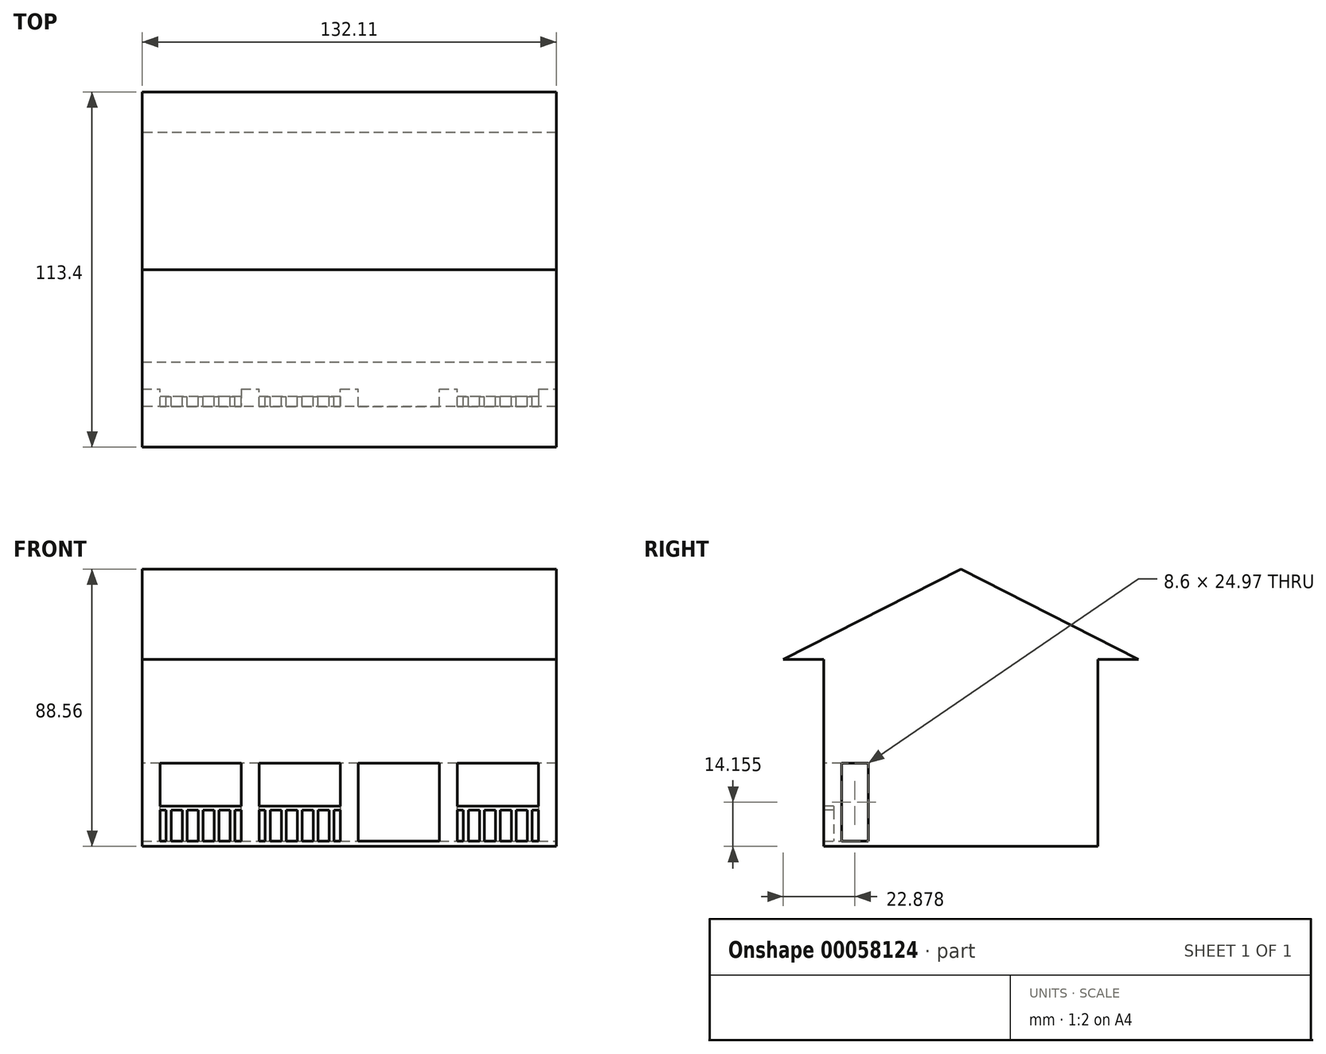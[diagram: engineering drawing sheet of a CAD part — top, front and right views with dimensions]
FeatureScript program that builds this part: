
annotation { "Feature Type Name" : "Feature", "Feature Type Description" : "" }
export const myFeature = defineFeature(function(context is Context, id is Id, definition is map)
    precondition{}
    {
        {
            var Q0;
            Q0=qCreatedBy(makeId("Right.planeOp"),FACE);
            var sketch = newSketch(context, id + "F0", { "sketchPlane" : qUnion([Q0])});
            skLineSegment(sketch, "E0.bottom", {"start": v(-28.53, -15.4) * mm, "end": v(58.95, -15.4) * mm});
            skLineSegment(sketch, "E0.top", {"start": v(-28.53, 44.37) * mm, "end": v(58.95, 44.37) * mm});
            skLineSegment(sketch, "E0.left", {"start": v(-28.53, -15.4) * mm, "end": v(-28.53, 44.37) * mm});
            skLineSegment(sketch, "E0.right", {"start": v(58.95, -15.4) * mm, "end": v(58.95, 44.37) * mm});
            skLineSegment(sketch, "E1", {"start": v(-28.53, 44.37) * mm, "end": v(-41.49, 44.37) * mm});
            skLineSegment(sketch, "E2", {"start": v(-41.49, 44.37) * mm, "end": v(15.2, 73.17) * mm});
            skLineSegment(sketch, "E3", {"start": v(15.2, 73.17) * mm, "end": v(71.9, 44.37) * mm});
            skLineSegment(sketch, "E4", {"start": v(71.9, 44.37) * mm, "end": v(58.95, 44.37) * mm});
            skLineSegment(sketch, "E5", {"start": v(-14.3, -15.4) * mm, "end": v(-14.3, 11.25) * mm});
            skLineSegment(sketch, "E6", {"start": v(-14.3, 11.25) * mm, "end": v(-28.53, 11.25) * mm});
            skSolve(sketch);
        }
        {
            var Q0;
            Q0=makeQuery(id+"F0.imprint","IMPRINT",FACE,{"disambiguationData":[TD([[makeQuery(id+"F0.imprint","IMPRINT",EDGE,{"derivedFrom":sQuery(id+"F0.wireOp",EDGE,"E0.top")}),1.0]])]});
            var Q1;
            {var subQ2=sQuery(id+"F0.wireOp",EDGE,"E0.top");Q1=makeQuery(id+"F0.imprint","IMPRINT",FACE,{"disambiguationData":[TD([[makeQuery(id+"F0.imprint","IMPRINT",EDGE,{"derivedFrom":subQ2}),-1.0]])]});}
            extrude(context, id + "F1", {"entities" : qUnion([Q0, Q1]), "depth" : 132.11 * mm});
        }
        {
            var Q0;
            Q0=makeQuery(id+"F1.opExtrude","SWEPT_FACE",FACE,{"disambiguationData":[OSD([sQuery(id+"F0.wireOp",EDGE,"E5")])]});
            var sketch = newSketch(context, id + "F2", { "sketchPlane" : qUnion([Q0])});
            skLineSegment(sketch, "E7.bottom", {"start": v(0, -15.4) * mm, "end": v(132.11, -15.4) * mm});
            skLineSegment(sketch, "E7.top", {"start": v(0, -13.72) * mm, "end": v(132.11, -13.72) * mm});
            skLineSegment(sketch, "E7.left", {"start": v(0, -15.4) * mm, "end": v(0, -13.72) * mm});
            skLineSegment(sketch, "E7.right", {"start": v(132.11, -15.4) * mm, "end": v(132.11, -13.72) * mm});
            skSolve(sketch);
        }
        {
            var Q0;
            Q0=makeQuery(id+"F2.imprint","IMPRINT",FACE,{"disambiguationData":[TD([[makeQuery(id+"F2.imprint","IMPRINT",EDGE,{"derivedFrom":sQuery(id+"F2.wireOp",EDGE,"E7.bottom")}),-1.0]])]});
            var Q1;
            Q1=makeQuery(id+"F1.opExtrude","SWEPT_FACE",FACE,{"disambiguationData":[OSD([sQuery(id+"F0.wireOp",EDGE,"E0.left")])]});
            extrude(context, id + "F3", {"entities" : qUnion([Q0]), "operationType" : NewBodyOperationType.ADD, "endBound" : BoundingType.UP_TO_SURFACE, "endBoundEntityFace" : qUnion([Q1]), "depth" : 25.4 * mm});
        }
        {
            var Q0;
            Q0=makeQuery(id+"F3.opExtrude","SWEPT_FACE",FACE,{"disambiguationData":[OSD([sQuery(id+"F2.wireOp",EDGE,"E7.top")])]});
            var sketch = newSketch(context, id + "F4", { "sketchPlane" : qUnion([Q0])});
            skLineSegment(sketch, "E8.bottom", {"start": v(0, -28.53) * mm, "end": v(5.62, -28.53) * mm});
            skLineSegment(sketch, "E8.top", {"start": v(0, -22.91) * mm, "end": v(5.62, -22.91) * mm});
            skLineSegment(sketch, "E8.left", {"start": v(0, -28.53) * mm, "end": v(0, -22.91) * mm});
            skLineSegment(sketch, "E8.right", {"start": v(5.62, -28.53) * mm, "end": v(5.62, -22.91) * mm});
            skLineSegment(sketch, "E9.1.0.0", {"start": v(31.62, -28.53) * mm, "end": v(37.24, -28.53) * mm});
            skLineSegment(sketch, "E9.1.0.1", {"start": v(31.62, -22.91) * mm, "end": v(37.24, -22.91) * mm});
            skLineSegment(sketch, "E9.1.0.2", {"start": v(31.62, -28.53) * mm, "end": v(31.62, -22.91) * mm});
            skLineSegment(sketch, "E9.1.0.3", {"start": v(37.24, -28.53) * mm, "end": v(37.24, -22.91) * mm});
            skLineSegment(sketch, "E9.2.0.0", {"start": v(63.25, -28.53) * mm, "end": v(68.86, -28.53) * mm});
            skLineSegment(sketch, "E9.2.0.1", {"start": v(63.25, -22.91) * mm, "end": v(68.86, -22.91) * mm});
            skLineSegment(sketch, "E9.2.0.2", {"start": v(63.25, -28.53) * mm, "end": v(63.25, -22.91) * mm});
            skLineSegment(sketch, "E9.2.0.3", {"start": v(68.86, -28.53) * mm, "end": v(68.86, -22.91) * mm});
            skLineSegment(sketch, "E9.3.0.0", {"start": v(94.87, -28.53) * mm, "end": v(100.49, -28.53) * mm});
            skLineSegment(sketch, "E9.3.0.1", {"start": v(94.87, -22.91) * mm, "end": v(100.49, -22.91) * mm});
            skLineSegment(sketch, "E9.3.0.2", {"start": v(94.87, -28.53) * mm, "end": v(94.87, -22.91) * mm});
            skLineSegment(sketch, "E9.3.0.3", {"start": v(100.49, -28.53) * mm, "end": v(100.49, -22.91) * mm});
            skLineSegment(sketch, "E9.4.0.0", {"start": v(126.5, -28.53) * mm, "end": v(132.11, -28.53) * mm});
            skLineSegment(sketch, "E9.4.0.1", {"start": v(126.5, -22.91) * mm, "end": v(132.11, -22.91) * mm});
            skLineSegment(sketch, "E9.4.0.2", {"start": v(126.5, -28.53) * mm, "end": v(126.5, -22.91) * mm});
            skLineSegment(sketch, "E9.4.0.3", {"start": v(132.11, -28.53) * mm, "end": v(132.11, -22.91) * mm});
            skLineSegment(sketch, "E9.direction1", {"start": v(0, -28.53) * mm, "end": v(31.62, -28.53) * mm, "construction": true});
            skLineSegment(sketch, "E10.bottom", {"start": v(7.63, -28.53) * mm, "end": v(9.26, -28.53) * mm});
            skLineSegment(sketch, "E10.top", {"start": v(7.63, -25.42) * mm, "end": v(9.26, -25.42) * mm});
            skLineSegment(sketch, "E10.left", {"start": v(7.63, -28.53) * mm, "end": v(7.63, -25.42) * mm});
            skLineSegment(sketch, "E10.right", {"start": v(9.26, -28.53) * mm, "end": v(9.26, -25.42) * mm});
            skLineSegment(sketch, "E11.1.0.0", {"start": v(12.72, -25.42) * mm, "end": v(14.35, -25.42) * mm});
            skLineSegment(sketch, "E11.1.0.1", {"start": v(12.72, -28.53) * mm, "end": v(14.35, -28.53) * mm});
            skLineSegment(sketch, "E11.1.0.2", {"start": v(14.35, -28.53) * mm, "end": v(14.35, -25.42) * mm});
            skLineSegment(sketch, "E11.1.0.3", {"start": v(12.72, -28.53) * mm, "end": v(12.72, -25.42) * mm});
            skLineSegment(sketch, "E11.2.0.0", {"start": v(17.8, -25.42) * mm, "end": v(19.43, -25.42) * mm});
            skLineSegment(sketch, "E11.2.0.1", {"start": v(17.8, -28.53) * mm, "end": v(19.43, -28.53) * mm});
            skLineSegment(sketch, "E11.2.0.2", {"start": v(19.43, -28.53) * mm, "end": v(19.43, -25.42) * mm});
            skLineSegment(sketch, "E11.2.0.3", {"start": v(17.8, -28.53) * mm, "end": v(17.8, -25.42) * mm});
            skLineSegment(sketch, "E11.3.0.0", {"start": v(22.9, -25.42) * mm, "end": v(24.52, -25.42) * mm});
            skLineSegment(sketch, "E11.3.0.1", {"start": v(22.9, -28.53) * mm, "end": v(24.52, -28.53) * mm});
            skLineSegment(sketch, "E11.3.0.2", {"start": v(24.52, -28.53) * mm, "end": v(24.52, -25.42) * mm});
            skLineSegment(sketch, "E11.3.0.3", {"start": v(22.9, -28.53) * mm, "end": v(22.9, -25.42) * mm});
            skLineSegment(sketch, "E11.4.0.0", {"start": v(27.98, -25.42) * mm, "end": v(29.6, -25.42) * mm});
            skLineSegment(sketch, "E11.4.0.1", {"start": v(27.98, -28.53) * mm, "end": v(29.6, -28.53) * mm});
            skLineSegment(sketch, "E11.4.0.2", {"start": v(29.6, -28.53) * mm, "end": v(29.6, -25.42) * mm});
            skLineSegment(sketch, "E11.4.0.3", {"start": v(27.98, -28.53) * mm, "end": v(27.98, -25.42) * mm});
            skLineSegment(sketch, "E11.direction1", {"start": v(7.63, -25.42) * mm, "end": v(12.72, -25.42) * mm, "construction": true});
            skLineSegment(sketch, "E12", {"start": v(7.63, -25.42) * mm, "end": v(5.62, -25.42) * mm, "construction": true});
            skLineSegment(sketch, "E13", {"start": v(29.6, -25.42) * mm, "end": v(31.62, -25.42) * mm, "construction": true});
            skLineSegment(sketch, "E14.1.0.0", {"start": v(44.34, -28.53) * mm, "end": v(45.97, -28.53) * mm});
            skLineSegment(sketch, "E14.1.0.1", {"start": v(49.43, -25.42) * mm, "end": v(51.06, -25.42) * mm});
            skLineSegment(sketch, "E14.1.0.2", {"start": v(39.26, -25.42) * mm, "end": v(44.34, -25.42) * mm, "construction": true});
            skLineSegment(sketch, "E14.1.0.3", {"start": v(44.34, -25.42) * mm, "end": v(45.97, -25.42) * mm});
            skLineSegment(sketch, "E14.1.0.4", {"start": v(54.51, -28.53) * mm, "end": v(56.14, -28.53) * mm});
            skLineSegment(sketch, "E14.1.0.5", {"start": v(54.51, -25.42) * mm, "end": v(56.14, -25.42) * mm});
            skLineSegment(sketch, "E14.1.0.6", {"start": v(59.6, -28.53) * mm, "end": v(59.6, -25.42) * mm});
            skLineSegment(sketch, "E14.1.0.7", {"start": v(39.26, -28.53) * mm, "end": v(40.89, -28.53) * mm});
            skLineSegment(sketch, "E14.1.0.8", {"start": v(39.26, -28.53) * mm, "end": v(39.26, -25.42) * mm});
            skLineSegment(sketch, "E14.1.0.9", {"start": v(59.6, -25.42) * mm, "end": v(61.23, -25.42) * mm});
            skLineSegment(sketch, "E14.1.0.10", {"start": v(49.43, -28.53) * mm, "end": v(51.06, -28.53) * mm});
            skLineSegment(sketch, "E14.1.0.11", {"start": v(59.6, -28.53) * mm, "end": v(61.23, -28.53) * mm});
            skLineSegment(sketch, "E14.1.0.12", {"start": v(39.26, -25.42) * mm, "end": v(40.89, -25.42) * mm});
            skLineSegment(sketch, "E14.1.0.13", {"start": v(49.43, -28.53) * mm, "end": v(49.43, -25.42) * mm});
            skLineSegment(sketch, "E14.1.0.14", {"start": v(45.97, -28.53) * mm, "end": v(45.97, -25.42) * mm});
            skLineSegment(sketch, "E14.1.0.15", {"start": v(54.51, -28.53) * mm, "end": v(54.51, -25.42) * mm});
            skLineSegment(sketch, "E14.1.0.16", {"start": v(56.14, -28.53) * mm, "end": v(56.14, -25.42) * mm});
            skLineSegment(sketch, "E14.1.0.17", {"start": v(40.89, -28.53) * mm, "end": v(40.89, -25.42) * mm});
            skLineSegment(sketch, "E14.1.0.18", {"start": v(61.23, -28.53) * mm, "end": v(61.23, -25.42) * mm});
            skLineSegment(sketch, "E14.1.0.19", {"start": v(44.34, -28.53) * mm, "end": v(44.34, -25.42) * mm});
            skLineSegment(sketch, "E14.1.0.20", {"start": v(51.06, -28.53) * mm, "end": v(51.06, -25.42) * mm});
            skLineSegment(sketch, "E14.2.0.0", {"start": v(75.97, -28.53) * mm, "end": v(77.6, -28.53) * mm});
            skLineSegment(sketch, "E14.2.0.1", {"start": v(81.05, -25.42) * mm, "end": v(82.68, -25.42) * mm});
            skLineSegment(sketch, "E14.2.0.2", {"start": v(70.88, -25.42) * mm, "end": v(75.97, -25.42) * mm, "construction": true});
            skLineSegment(sketch, "E14.2.0.3", {"start": v(75.97, -25.42) * mm, "end": v(77.6, -25.42) * mm});
            skLineSegment(sketch, "E14.2.0.4", {"start": v(86.14, -28.53) * mm, "end": v(87.77, -28.53) * mm});
            skLineSegment(sketch, "E14.2.0.5", {"start": v(86.14, -25.42) * mm, "end": v(87.77, -25.42) * mm});
            skLineSegment(sketch, "E14.2.0.6", {"start": v(91.22, -28.53) * mm, "end": v(91.22, -25.42) * mm});
            skLineSegment(sketch, "E14.2.0.7", {"start": v(70.88, -28.53) * mm, "end": v(72.5, -28.53) * mm});
            skLineSegment(sketch, "E14.2.0.8", {"start": v(70.88, -28.53) * mm, "end": v(70.88, -25.42) * mm});
            skLineSegment(sketch, "E14.2.0.9", {"start": v(91.22, -25.42) * mm, "end": v(92.85, -25.42) * mm});
            skLineSegment(sketch, "E14.2.0.10", {"start": v(81.05, -28.53) * mm, "end": v(82.68, -28.53) * mm});
            skLineSegment(sketch, "E14.2.0.11", {"start": v(91.22, -28.53) * mm, "end": v(92.85, -28.53) * mm});
            skLineSegment(sketch, "E14.2.0.12", {"start": v(70.88, -25.42) * mm, "end": v(72.5, -25.42) * mm});
            skLineSegment(sketch, "E14.2.0.13", {"start": v(81.05, -28.53) * mm, "end": v(81.05, -25.42) * mm});
            skLineSegment(sketch, "E14.2.0.14", {"start": v(77.6, -28.53) * mm, "end": v(77.6, -25.42) * mm});
            skLineSegment(sketch, "E14.2.0.15", {"start": v(86.14, -28.53) * mm, "end": v(86.14, -25.42) * mm});
            skLineSegment(sketch, "E14.2.0.16", {"start": v(87.77, -28.53) * mm, "end": v(87.77, -25.42) * mm});
            skLineSegment(sketch, "E14.2.0.17", {"start": v(72.5, -28.53) * mm, "end": v(72.5, -25.42) * mm});
            skLineSegment(sketch, "E14.2.0.18", {"start": v(92.85, -28.53) * mm, "end": v(92.85, -25.42) * mm});
            skLineSegment(sketch, "E14.2.0.19", {"start": v(75.97, -28.53) * mm, "end": v(75.97, -25.42) * mm});
            skLineSegment(sketch, "E14.2.0.20", {"start": v(82.68, -28.53) * mm, "end": v(82.68, -25.42) * mm});
            skLineSegment(sketch, "E14.3.0.0", {"start": v(107.59, -28.53) * mm, "end": v(109.22, -28.53) * mm});
            skLineSegment(sketch, "E14.3.0.1", {"start": v(112.68, -25.42) * mm, "end": v(114.3, -25.42) * mm});
            skLineSegment(sketch, "E14.3.0.2", {"start": v(102.5, -25.42) * mm, "end": v(107.59, -25.42) * mm, "construction": true});
            skLineSegment(sketch, "E14.3.0.3", {"start": v(107.59, -25.42) * mm, "end": v(109.22, -25.42) * mm});
            skLineSegment(sketch, "E14.3.0.4", {"start": v(117.76, -28.53) * mm, "end": v(119.4, -28.53) * mm});
            skLineSegment(sketch, "E14.3.0.5", {"start": v(117.76, -25.42) * mm, "end": v(119.4, -25.42) * mm});
            skLineSegment(sketch, "E14.3.0.6", {"start": v(122.85, -28.53) * mm, "end": v(122.85, -25.42) * mm});
            skLineSegment(sketch, "E14.3.0.7", {"start": v(102.5, -28.53) * mm, "end": v(104.13, -28.53) * mm});
            skLineSegment(sketch, "E14.3.0.8", {"start": v(102.5, -28.53) * mm, "end": v(102.5, -25.42) * mm});
            skLineSegment(sketch, "E14.3.0.9", {"start": v(122.85, -25.42) * mm, "end": v(124.48, -25.42) * mm});
            skLineSegment(sketch, "E14.3.0.10", {"start": v(112.68, -28.53) * mm, "end": v(114.3, -28.53) * mm});
            skLineSegment(sketch, "E14.3.0.11", {"start": v(122.85, -28.53) * mm, "end": v(124.48, -28.53) * mm});
            skLineSegment(sketch, "E14.3.0.12", {"start": v(102.5, -25.42) * mm, "end": v(104.13, -25.42) * mm});
            skLineSegment(sketch, "E14.3.0.13", {"start": v(112.68, -28.53) * mm, "end": v(112.68, -25.42) * mm});
            skLineSegment(sketch, "E14.3.0.14", {"start": v(109.22, -28.53) * mm, "end": v(109.22, -25.42) * mm});
            skLineSegment(sketch, "E14.3.0.15", {"start": v(117.76, -28.53) * mm, "end": v(117.76, -25.42) * mm});
            skLineSegment(sketch, "E14.3.0.16", {"start": v(119.4, -28.53) * mm, "end": v(119.4, -25.42) * mm});
            skLineSegment(sketch, "E14.3.0.17", {"start": v(104.13, -28.53) * mm, "end": v(104.13, -25.42) * mm});
            skLineSegment(sketch, "E14.3.0.18", {"start": v(124.48, -28.53) * mm, "end": v(124.48, -25.42) * mm});
            skLineSegment(sketch, "E14.3.0.19", {"start": v(107.59, -28.53) * mm, "end": v(107.59, -25.42) * mm});
            skLineSegment(sketch, "E14.3.0.20", {"start": v(114.3, -28.53) * mm, "end": v(114.3, -25.42) * mm});
            skLineSegment(sketch, "E14.direction1", {"start": v(12.72, -28.53) * mm, "end": v(44.34, -28.53) * mm, "construction": true});
            skLineSegment(sketch, "E15", {"start": v(39.26, -25.42) * mm, "end": v(37.24, -25.42) * mm, "construction": true});
            skSolve(sketch);
        }
        {
            var Q0;
            Q0=makeQuery(id+"F4.imprint","IMPRINT",FACE,{"disambiguationData":[TD([[makeQuery(id+"F4.imprint","IMPRINT",EDGE,{"derivedFrom":sQuery(id+"F4.wireOp",EDGE,"E8.bottom")}),1.0]])]});
            var Q1;
            Q1=makeQuery(id+"F4.imprint","IMPRINT",FACE,{"disambiguationData":[TD([[makeQuery(id+"F4.imprint","IMPRINT",EDGE,{"derivedFrom":sQuery(id+"F4.wireOp",EDGE,"E9.1.0.0")}),1.0]])]});
            var Q2;
            Q2=makeQuery(id+"F4.imprint","IMPRINT",FACE,{"disambiguationData":[TD([[makeQuery(id+"F4.imprint","IMPRINT",EDGE,{"derivedFrom":sQuery(id+"F4.wireOp",EDGE,"E9.2.0.0")}),1.0]])]});
            var Q3;
            Q3=makeQuery(id+"F4.imprint","IMPRINT",FACE,{"disambiguationData":[TD([[makeQuery(id+"F4.imprint","IMPRINT",EDGE,{"derivedFrom":sQuery(id+"F4.wireOp",EDGE,"E9.3.0.0")}),1.0]])]});
            var Q4;
            Q4=makeQuery(id+"F4.imprint","IMPRINT",FACE,{"disambiguationData":[TD([[makeQuery(id+"F4.imprint","IMPRINT",EDGE,{"derivedFrom":sQuery(id+"F4.wireOp",EDGE,"E9.4.0.0")}),1.0]])]});
            extrude(context, id + "F5", {"entities" : qUnion([Q0, Q1, Q2, Q3, Q4]), "operationType" : NewBodyOperationType.ADD, "endBound" : BoundingType.UP_TO_NEXT, "depth" : 25.4 * mm});
        }
        {
            var Q0;
            Q0=makeQuery(id+"F4.imprint","IMPRINT",FACE,{"disambiguationData":[TD([[makeQuery(id+"F4.imprint","IMPRINT",EDGE,{"derivedFrom":sQuery(id+"F4.wireOp",EDGE,"E8.bottom")}),1.0]])]});
            var Q1;
            Q1=makeQuery(id+"F4.imprint","IMPRINT",FACE,{"disambiguationData":[TD([[makeQuery(id+"F4.imprint","IMPRINT",EDGE,{"derivedFrom":sQuery(id+"F4.wireOp",EDGE,"E9.1.0.0")}),1.0]])]});
            var Q2;
            Q2=makeQuery(id+"F4.imprint","IMPRINT",FACE,{"disambiguationData":[TD([[makeQuery(id+"F4.imprint","IMPRINT",EDGE,{"derivedFrom":sQuery(id+"F4.wireOp",EDGE,"E9.2.0.0")}),1.0]])]});
            var Q3;
            Q3=makeQuery(id+"F4.imprint","IMPRINT",FACE,{"disambiguationData":[TD([[makeQuery(id+"F4.imprint","IMPRINT",EDGE,{"derivedFrom":sQuery(id+"F4.wireOp",EDGE,"E9.3.0.0")}),1.0]])]});
            var Q4;
            Q4=makeQuery(id+"F4.imprint","IMPRINT",FACE,{"disambiguationData":[TD([[makeQuery(id+"F4.imprint","IMPRINT",EDGE,{"derivedFrom":sQuery(id+"F4.wireOp",EDGE,"E9.4.0.0")}),1.0]])]});
            var Q5;
            Q5=makeQuery(id+"F4.imprint","IMPRINT",FACE,{"disambiguationData":[TD([[makeQuery(id+"F4.imprint","IMPRINT",EDGE,{"derivedFrom":sQuery(id+"F4.wireOp",EDGE,"E10.bottom")}),1.0]])]});
            var Q6;
            Q6=makeQuery(id+"F4.imprint","IMPRINT",FACE,{"disambiguationData":[TD([[makeQuery(id+"F4.imprint","IMPRINT",EDGE,{"derivedFrom":sQuery(id+"F4.wireOp",EDGE,"E11.1.0.0")}),-1.0]])]});
            var Q7;
            Q7=makeQuery(id+"F4.imprint","IMPRINT",FACE,{"disambiguationData":[TD([[makeQuery(id+"F4.imprint","IMPRINT",EDGE,{"derivedFrom":sQuery(id+"F4.wireOp",EDGE,"E11.2.0.0")}),-1.0]])]});
            var Q8;
            Q8=makeQuery(id+"F4.imprint","IMPRINT",FACE,{"disambiguationData":[TD([[makeQuery(id+"F4.imprint","IMPRINT",EDGE,{"derivedFrom":sQuery(id+"F4.wireOp",EDGE,"E11.3.0.0")}),-1.0]])]});
            var Q9;
            Q9=makeQuery(id+"F4.imprint","IMPRINT",FACE,{"disambiguationData":[TD([[makeQuery(id+"F4.imprint","IMPRINT",EDGE,{"derivedFrom":sQuery(id+"F4.wireOp",EDGE,"E11.4.0.0")}),-1.0]])]});
            var Q10;
            Q10=makeQuery(id+"F4.imprint","IMPRINT",FACE,{"disambiguationData":[TD([[makeQuery(id+"F4.imprint","IMPRINT",EDGE,{"derivedFrom":sQuery(id+"F4.wireOp",EDGE,"E14.1.0.0")}),1.0]])]});
            var Q11;
            Q11=makeQuery(id+"F4.imprint","IMPRINT",FACE,{"disambiguationData":[TD([[makeQuery(id+"F4.imprint","IMPRINT",EDGE,{"derivedFrom":sQuery(id+"F4.wireOp",EDGE,"E14.1.0.1")}),-1.0]])]});
            var Q12;
            Q12=makeQuery(id+"F4.imprint","IMPRINT",FACE,{"disambiguationData":[TD([[makeQuery(id+"F4.imprint","IMPRINT",EDGE,{"derivedFrom":sQuery(id+"F4.wireOp",EDGE,"E14.1.0.4")}),1.0]])]});
            var Q13;
            Q13=makeQuery(id+"F4.imprint","IMPRINT",FACE,{"disambiguationData":[TD([[makeQuery(id+"F4.imprint","IMPRINT",EDGE,{"derivedFrom":sQuery(id+"F4.wireOp",EDGE,"E14.1.0.6")}),-1.0]])]});
            var Q14;
            Q14=makeQuery(id+"F4.imprint","IMPRINT",FACE,{"disambiguationData":[TD([[makeQuery(id+"F4.imprint","IMPRINT",EDGE,{"derivedFrom":sQuery(id+"F4.wireOp",EDGE,"E14.1.0.7")}),1.0]])]});
            var Q15;
            Q15=makeQuery(id+"F4.imprint","IMPRINT",FACE,{"disambiguationData":[TD([[makeQuery(id+"F4.imprint","IMPRINT",EDGE,{"derivedFrom":sQuery(id+"F4.wireOp",EDGE,"E14.3.0.0")}),1.0]])]});
            var Q16;
            Q16=makeQuery(id+"F4.imprint","IMPRINT",FACE,{"disambiguationData":[TD([[makeQuery(id+"F4.imprint","IMPRINT",EDGE,{"derivedFrom":sQuery(id+"F4.wireOp",EDGE,"E14.3.0.1")}),-1.0]])]});
            var Q17;
            Q17=makeQuery(id+"F4.imprint","IMPRINT",FACE,{"disambiguationData":[TD([[makeQuery(id+"F4.imprint","IMPRINT",EDGE,{"derivedFrom":sQuery(id+"F4.wireOp",EDGE,"E14.3.0.4")}),1.0]])]});
            var Q18;
            Q18=makeQuery(id+"F4.imprint","IMPRINT",FACE,{"disambiguationData":[TD([[makeQuery(id+"F4.imprint","IMPRINT",EDGE,{"derivedFrom":sQuery(id+"F4.wireOp",EDGE,"E14.3.0.6")}),-1.0]])]});
            var Q19;
            Q19=makeQuery(id+"F4.imprint","IMPRINT",FACE,{"disambiguationData":[TD([[makeQuery(id+"F4.imprint","IMPRINT",EDGE,{"derivedFrom":sQuery(id+"F4.wireOp",EDGE,"E14.3.0.7")}),1.0]])]});
            extrude(context, id + "F6", {"entities" : qUnion([Q0, Q1, Q2, Q3, Q4, Q5, Q6, Q7, Q8, Q9, Q10, Q11, Q12, Q13, Q14, Q15, Q16, Q17, Q18, Q19]), "operationType" : NewBodyOperationType.ADD, "depth" : 10 * mm});
        }
        {
            var Q0;
            Q0=makeQuery(id+"F5.opExtrude","SWEPT_FACE",FACE,{"disambiguationData":[OSD([sQuery(id+"F4.wireOp",EDGE,"E8.right")])]});
            var sketch = newSketch(context, id + "F7", { "sketchPlane" : qUnion([Q0])});
            skLineSegment(sketch, "E16.bottom", {"start": v(-28.53, -3.72) * mm, "end": v(-25.42, -3.72) * mm});
            skLineSegment(sketch, "E16.top", {"start": v(-28.53, -2.48) * mm, "end": v(-25.42, -2.48) * mm});
            skLineSegment(sketch, "E16.left", {"start": v(-28.53, -3.72) * mm, "end": v(-28.53, -2.48) * mm});
            skLineSegment(sketch, "E16.right", {"start": v(-25.42, -3.72) * mm, "end": v(-25.42, -2.48) * mm});
            skSolve(sketch);
        }
        {
            var Q0;
            Q0=makeQuery(id+"F7.imprint","IMPRINT",FACE,{"disambiguationData":[TD([[makeQuery(id+"F7.imprint","IMPRINT",EDGE,{"derivedFrom":sQuery(id+"F7.wireOp",EDGE,"E16.bottom")}),1.0]])]});
            var Q1;
            Q1=makeQuery(id+"F5.opExtrude","SWEPT_FACE",FACE,{"disambiguationData":[OSD([sQuery(id+"F4.wireOp",EDGE,"E9.2.0.2")])]});
            extrude(context, id + "F8", {"entities" : qUnion([Q0]), "operationType" : NewBodyOperationType.ADD, "endBound" : BoundingType.UP_TO_SURFACE, "endBoundEntityFace" : qUnion([Q1]), "depth" : 25.4 * mm});
        }
        {
            var Q0;
            Q0=makeQuery(id+"F5.opExtrude","SWEPT_FACE",FACE,{"disambiguationData":[OSD([sQuery(id+"F4.wireOp",EDGE,"E9.3.0.3")])]});
            var sketch = newSketch(context, id + "F9", { "sketchPlane" : qUnion([Q0])});
            skLineSegment(sketch, "E17.0", {"start": v(-28.53, -2.48) * mm, "end": v(-25.42, -2.48) * mm});
            skLineSegment(sketch, "E17.1", {"start": v(-28.53, -3.72) * mm, "end": v(-28.53, -2.48) * mm});
            skLineSegment(sketch, "E17.2", {"start": v(-28.53, -3.72) * mm, "end": v(-25.42, -3.72) * mm});
            skLineSegment(sketch, "E17.3", {"start": v(-25.42, -3.72) * mm, "end": v(-25.42, -2.48) * mm});
            skSolve(sketch);
        }
        {
            var Q0;
            Q0 = qSketchRegion(id + "F9", true);
            extrude(context, id + "F10", {"entities" : qUnion([Q0]), "operationType" : NewBodyOperationType.ADD, "endBound" : BoundingType.UP_TO_NEXT, "depth" : 25.4 * mm});
        }
    });
